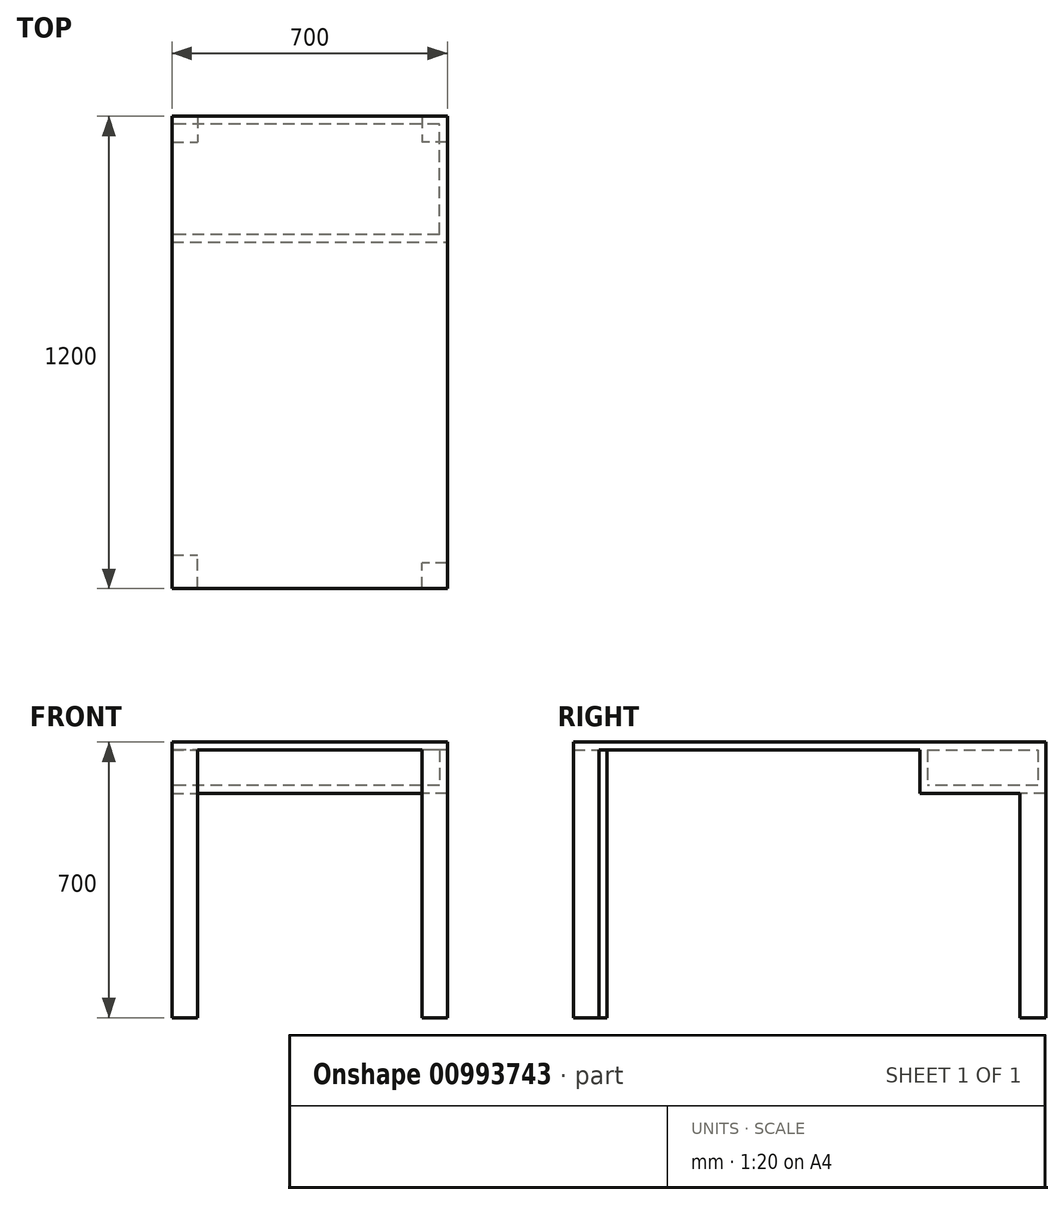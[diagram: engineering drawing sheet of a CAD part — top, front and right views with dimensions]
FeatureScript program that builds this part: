
annotation { "Feature Type Name" : "Feature", "Feature Type Description" : "" }
export const myFeature = defineFeature(function(context is Context, id is Id, definition is map)
    precondition{}
    {
        {
            var Q0;
            Q0=qCreatedBy(makeId("Top.planeOp"),FACE);
            var sketch = newSketch(context, id + "F0", { "sketchPlane" : qUnion([Q0])});
            skLineSegment(sketch, "E0.bottom", {"start": v(-97.07, 1130.42) * mm, "end": v(602.93, 1130.42) * mm});
            skLineSegment(sketch, "E0.top", {"start": v(-97.07, -69.58) * mm, "end": v(602.93, -69.58) * mm});
            skLineSegment(sketch, "E0.left", {"start": v(-97.07, 1130.42) * mm, "end": v(-97.07, -69.58) * mm});
            skLineSegment(sketch, "E0.right", {"start": v(602.93, 1130.42) * mm, "end": v(602.93, -69.58) * mm});
            skSolve(sketch);
        }
        {
            var Q0;
            Q0 = qSketchRegion(id + "F0", true);
            extrude(context, id + "F1", {"entities" : qUnion([Q0]), "depth" : 20 * mm, "offsetDistance" : 25 * mm});
        }
        {
            var Q0;
            Q0=makeQuery(id+"F1.opExtrude","CAP_FACE",FACE,{"disambiguationData":[OSD([sQuery(id+"F0.wireOp",EDGE,"E0.bottom"),sQuery(id+"F0.wireOp",EDGE,"E0.top"),sQuery(id+"F0.wireOp",EDGE,"E0.left"),sQuery(id+"F0.wireOp",EDGE,"E0.right")])],"isStart":true});
            var sketch = newSketch(context, id + "F2", { "sketchPlane" : qUnion([Q0])});
            skLineSegment(sketch, "E1.bottom", {"start": v(-97.07, -1130.42) * mm, "end": v(602.93, -1130.42) * mm});
            skLineSegment(sketch, "E1.top", {"start": v(-97.07, -810.42) * mm, "end": v(602.93, -810.42) * mm});
            skLineSegment(sketch, "E1.left", {"start": v(-97.07, -1130.42) * mm, "end": v(-97.07, -810.42) * mm});
            skLineSegment(sketch, "E1.right", {"start": v(602.93, -1130.42) * mm, "end": v(602.93, -810.42) * mm});
            skSolve(sketch);
        }
        {
            var Q0;
            Q0 = qSketchRegion(id + "F2", true);
            extrude(context, id + "F3", {"entities" : qUnion([Q0]), "operationType" : NewBodyOperationType.ADD, "depth" : 110 * mm, "offsetDistance" : 25 * mm});
        }
        {
            var Q0;
            Q0=makeQuery(id+"F3.boolean.opBoolean","MERGE",FACE,{"derivedFrom":[makeQuery(id+"F1.opExtrude","SWEPT_FACE",FACE,{"disambiguationData":[OSD([sQuery(id+"F0.wireOp",EDGE,"E0.left")])]}),makeQuery(id+"F3.opExtrude","SWEPT_FACE",FACE,{"disambiguationData":[OSD([sQuery(id+"F2.wireOp",EDGE,"E1.left")])]})]});
            var sketch = newSketch(context, id + "F4", { "sketchPlane" : qUnion([Q0])});
            skLineSegment(sketch, "E2", {"start": v(-810.42, 0) * mm, "end": v(-1130.42, 0) * mm});
            skPoint(sketch, "E2.endSnap0", {"position": v(-1130.42, -45) * mm});
            skLineSegment(sketch, "E3", {"start": v(-1130.42, 0) * mm, "end": v(-1130.42, -110) * mm});
            skLineSegment(sketch, "E4", {"start": v(-1130.42, -110) * mm, "end": v(-810.42, -110) * mm});
            skLineSegment(sketch, "E5", {"start": v(-810.42, -110) * mm, "end": v(-810.42, 0) * mm});
            skLineSegment(sketch, "E6", {"start": v(-1130.42, -55) * mm, "end": v(-1110.42, -55) * mm});
            skLineSegment(sketch, "E7", {"start": v(-1005.14, -110) * mm, "end": v(-1005.14, -90) * mm});
            skLineSegment(sketch, "E8", {"start": v(-810.42, -55) * mm, "end": v(-830.42, -55) * mm});
            skLineSegment(sketch, "E9.bottom", {"start": v(-1110.42, 0) * mm, "end": v(-830.42, 0) * mm});
            skLineSegment(sketch, "E9.top", {"start": v(-1110.42, -90) * mm, "end": v(-830.42, -90) * mm});
            skLineSegment(sketch, "E9.left", {"start": v(-1110.42, 0) * mm, "end": v(-1110.42, -90) * mm});
            skLineSegment(sketch, "E9.right", {"start": v(-830.42, 0) * mm, "end": v(-830.42, -90) * mm});
            skSolve(sketch);
        }
        {
            var Q0;
            {var subQ2=sQuery(id+"F4.wireOp",EDGE,"E2");var subQ7=sQuery(id+"F4.wireOp",EDGE,"E9.right");var subQ9=makeQuery(id+"F4.imprint","INTERSECT",VERTEX,{"derivedFrom":[subQ2,subQ7]});Q0=makeQuery(id+"F4.imprint","IMPRINT",FACE,{"disambiguationData":[TD([[makeQuery(id+"F4.imprint","IMPRINT",EDGE,{"disambiguationData":[TD([[subQ9,-1.0]])],"derivedFrom":subQ2}),1.0]])]});}
            extrude(context, id + "F5", {"entities" : qUnion([Q0]), "operationType" : NewBodyOperationType.REMOVE, "oppositeDirection" : true, "depth" : 680 * mm, "offsetDistance" : 25 * mm});
        }
        {
            var Q0;
            Q0=makeQuery(id+"F1.opExtrude","CAP_FACE",FACE,{"disambiguationData":[OSD([sQuery(id+"F0.wireOp",EDGE,"E0.bottom"),sQuery(id+"F0.wireOp",EDGE,"E0.top"),sQuery(id+"F0.wireOp",EDGE,"E0.left"),sQuery(id+"F0.wireOp",EDGE,"E0.right")])],"isStart":true});
            var sketch = newSketch(context, id + "F6", { "sketchPlane" : qUnion([Q0])});
            skLineSegment(sketch, "E10.bottom", {"start": v(-97.07, 69.58) * mm, "end": v(-32.07, 69.58) * mm});
            skLineSegment(sketch, "E10.top", {"start": v(-97.07, -16.14) * mm, "end": v(-32.07, -16.14) * mm});
            skLineSegment(sketch, "E10.left", {"start": v(-97.07, 69.58) * mm, "end": v(-97.07, -16.14) * mm});
            skLineSegment(sketch, "E10.right", {"start": v(-32.07, 69.58) * mm, "end": v(-32.07, -16.14) * mm});
            skLineSegment(sketch, "E11.bottom", {"start": v(602.93, 69.58) * mm, "end": v(537.93, 69.58) * mm});
            skLineSegment(sketch, "E11.top", {"start": v(602.93, 4.58) * mm, "end": v(537.93, 4.58) * mm});
            skLineSegment(sketch, "E11.left", {"start": v(602.93, 69.58) * mm, "end": v(602.93, 4.58) * mm});
            skLineSegment(sketch, "E11.right", {"start": v(537.93, 69.58) * mm, "end": v(537.93, 4.58) * mm});
            skSolve(sketch);
        }
        {
            var Q0;
            Q0 = qSketchRegion(id + "F6", true);
            extrude(context, id + "F7", {"entities" : qUnion([Q0]), "operationType" : NewBodyOperationType.ADD, "depth" : 680 * mm, "offsetDistance" : 25 * mm});
        }
        {
            var Q0;
            Q0=makeQuery(id+"F3.opExtrude","CAP_FACE",FACE,{"disambiguationData":[OSD([sQuery(id+"F2.wireOp",EDGE,"E1.bottom"),sQuery(id+"F2.wireOp",EDGE,"E1.top"),sQuery(id+"F2.wireOp",EDGE,"E1.left"),sQuery(id+"F2.wireOp",EDGE,"E1.right")])],"isStart":false});
            var sketch = newSketch(context, id + "F8", { "sketchPlane" : qUnion([Q0])});
            skLineSegment(sketch, "E12.bottom", {"start": v(-97.07, -1130.42) * mm, "end": v(-32.07, -1130.42) * mm});
            skLineSegment(sketch, "E12.top", {"start": v(-97.07, -1065.42) * mm, "end": v(-32.07, -1065.42) * mm});
            skLineSegment(sketch, "E12.left", {"start": v(-97.07, -1130.42) * mm, "end": v(-97.07, -1065.42) * mm});
            skLineSegment(sketch, "E12.right", {"start": v(-32.07, -1130.42) * mm, "end": v(-32.07, -1065.42) * mm});
            skLineSegment(sketch, "E13.bottom", {"start": v(602.93, -1130.42) * mm, "end": v(537.93, -1130.42) * mm});
            skLineSegment(sketch, "E13.top", {"start": v(602.93, -1065.42) * mm, "end": v(537.93, -1065.42) * mm});
            skLineSegment(sketch, "E13.left", {"start": v(602.93, -1130.42) * mm, "end": v(602.93, -1065.42) * mm});
            skLineSegment(sketch, "E13.right", {"start": v(537.93, -1130.42) * mm, "end": v(537.93, -1065.42) * mm});
            skSolve(sketch);
        }
        {
            var Q0;
            Q0 = qSketchRegion(id + "F8", true);
            extrude(context, id + "F9", {"entities" : qUnion([Q0]), "operationType" : NewBodyOperationType.ADD, "depth" : 570 * mm, "offsetDistance" : 25 * mm});
        }
    });
